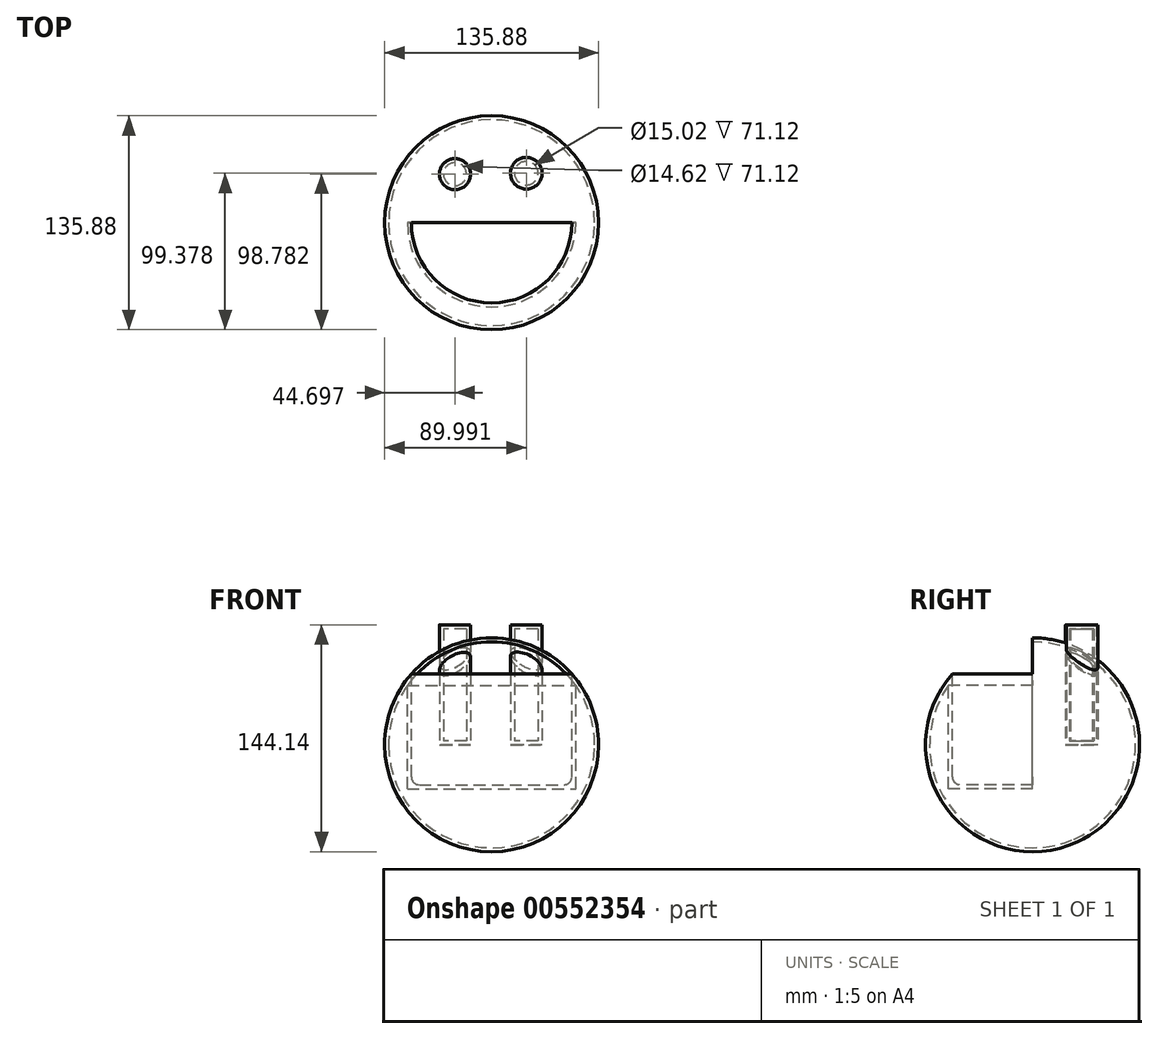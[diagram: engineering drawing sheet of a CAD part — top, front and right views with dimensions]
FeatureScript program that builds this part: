
annotation { "Feature Type Name" : "Feature", "Feature Type Description" : "" }
export const myFeature = defineFeature(function(context is Context, id is Id, definition is map)
    precondition{}
    {
        {
            var Q0;
            Q0=qCreatedBy(makeId("Top.planeOp"),FACE);
            var sketch = newSketch(context, id + "F0", { "sketchPlane" : qUnion([Q0])});
            skArc(sketch, "E0", {"start": v(-67.94, 0) * mm, "mid": v(0, -67.94) * mm, "end": v(67.94, 0) * mm});
            skLineSegment(sketch, "E1", {"start": v(-67.94, 0) * mm, "end": v(67.94, 0) * mm});
            skSolve(sketch);
        }
        {
            var Q0;
            Q0=makeQuery(id+"F0.imprint","IMPRINT",FACE,{"disambiguationData":[TD([[makeQuery(id+"F0.imprint","IMPRINT",EDGE,{"derivedFrom":sQuery(id+"F0.wireOp",EDGE,"E0")}),1.0]])]});
            var Q1;
            Q1=sQuery(id+"F0.wireOp",EDGE,"E1");
            revolve(context, id + "F1", {"entities" : qUnion([Q0]), "axis" : qUnion([Q1]), "revolveType" : RevolveType.FULL});
        }
        {
            var Q0;
            Q0=qCreatedBy(makeId("Top.planeOp"),FACE);
            var sketch = newSketch(context, id + "F2", { "sketchPlane" : qUnion([Q0])});
            skArc(sketch, "E2", {"start": v(-50.96, 0) * mm, "mid": v(0, -50.96) * mm, "end": v(50.96, 0) * mm});
            skLineSegment(sketch, "E3", {"start": v(-50.96, 0) * mm, "end": v(50.96, 0) * mm});
            skSolve(sketch);
        }
        {
            var Q0;
            Q0 = qSketchRegion(id + "F2", true);
            extrude(context, id + "F3", {"entities" : qUnion([Q0]), "operationType" : NewBodyOperationType.ADD, "depth" : 127 * mm, "offsetDistance" : 25.4 * mm});
        }
        {
            var Q0;
            Q0=makeQuery(id+"F3.opExtrude","CAP_FACE",FACE,{"disambiguationData":[OSD([sQuery(id+"F2.wireOp",EDGE,"E2"),sQuery(id+"F2.wireOp",EDGE,"E3")])],"isStart":false});
            var sketch = newSketch(context, id + "F4", { "sketchPlane" : qUnion([Q0])});
            skArc(sketch, "E4", {"start": v(-50.96, 0) * mm, "mid": v(0, -50.96) * mm, "end": v(50.96, 0) * mm});
            skLineSegment(sketch, "E5", {"start": v(-50.96, 0) * mm, "end": v(50.96, 0) * mm});
            skSolve(sketch);
        }
        {
            var Q0;
            Q0 = qSketchRegion(id + "F4", true);
            extrude(context, id + "F5", {"entities" : qUnion([Q0]), "operationType" : NewBodyOperationType.REMOVE, "oppositeDirection" : true, "depth" : 152.4 * mm, "offsetDistance" : 25.4 * mm});
        }
        {
            var Q0;
            Q0=makeQuery(id+"F5.boolean.opBoolean","COPY",FACE,{"derivedFrom":makeQuery(id+"F5.opExtrude","SWEPT_FACE",FACE,{"disambiguationData":[OSD([sQuery(id+"F4.wireOp",EDGE,"E5")])]})});
            shell(context, id + "F6", {"entities" : qUnion([Q0]), "thickness" : 2.54 * mm});
        }
        {
            var Q0;
            Q0=qCreatedBy(makeId("Top.planeOp"),FACE);
            var sketch = newSketch(context, id + "F7", { "sketchPlane" : qUnion([Q0])});
            skCircle(sketch, "E6", {"center": v(-23.24, 30.84) * mm, "radius": 9.85 * mm});
            skSolve(sketch);
        }
        {
            var Q0;
            Q0 = qSketchRegion(id + "F7", true);
            extrude(context, id + "F8", {"entities" : qUnion([Q0]), "operationType" : NewBodyOperationType.ADD, "depth" : 76.2 * mm, "offsetDistance" : 25.4 * mm});
        }
        {
            var Q0;
            Q0=qCreatedBy(makeId("Top.planeOp"),FACE);
            var sketch = newSketch(context, id + "F9", { "sketchPlane" : qUnion([Q0])});
            skCircle(sketch, "E7", {"center": v(22.05, 31.44) * mm, "radius": 10.05 * mm});
            skSolve(sketch);
        }
        {
            var Q0;
            Q0 = qSketchRegion(id + "F9", true);
            extrude(context, id + "F10", {"entities" : qUnion([Q0]), "operationType" : NewBodyOperationType.ADD, "depth" : 76.2 * mm, "offsetDistance" : 25.4 * mm});
        }
        {
            var Q0;
            Q0=makeQuery(id+"F1.opRevolve","SWEPT_FACE",FACE,{"disambiguationData":[OSD([sQuery(id+"F0.wireOp",EDGE,"E0")])]});
            shell(context, id + "F11", {"entities" : qUnion([Q0]), "thickness" : 2.54 * mm});
        }
        {
            var Q0;
            Q0=makeQuery(id+"F5.boolean.opBoolean","COPY",EDGE,{"derivedFrom":makeQuery(id+"F5.opExtrude","CAP_EDGE",EDGE,{"disambiguationData":[OSD([sQuery(id+"F4.wireOp",EDGE,"E4")])],"isStart":false})});
            fillet(context, id + "F12", {"entities" : qUnion([Q0]), "radius" : 5.08 * mm, "tangentPropagation" : true, "allowEdgeOverflow" : false});
        }
    });
